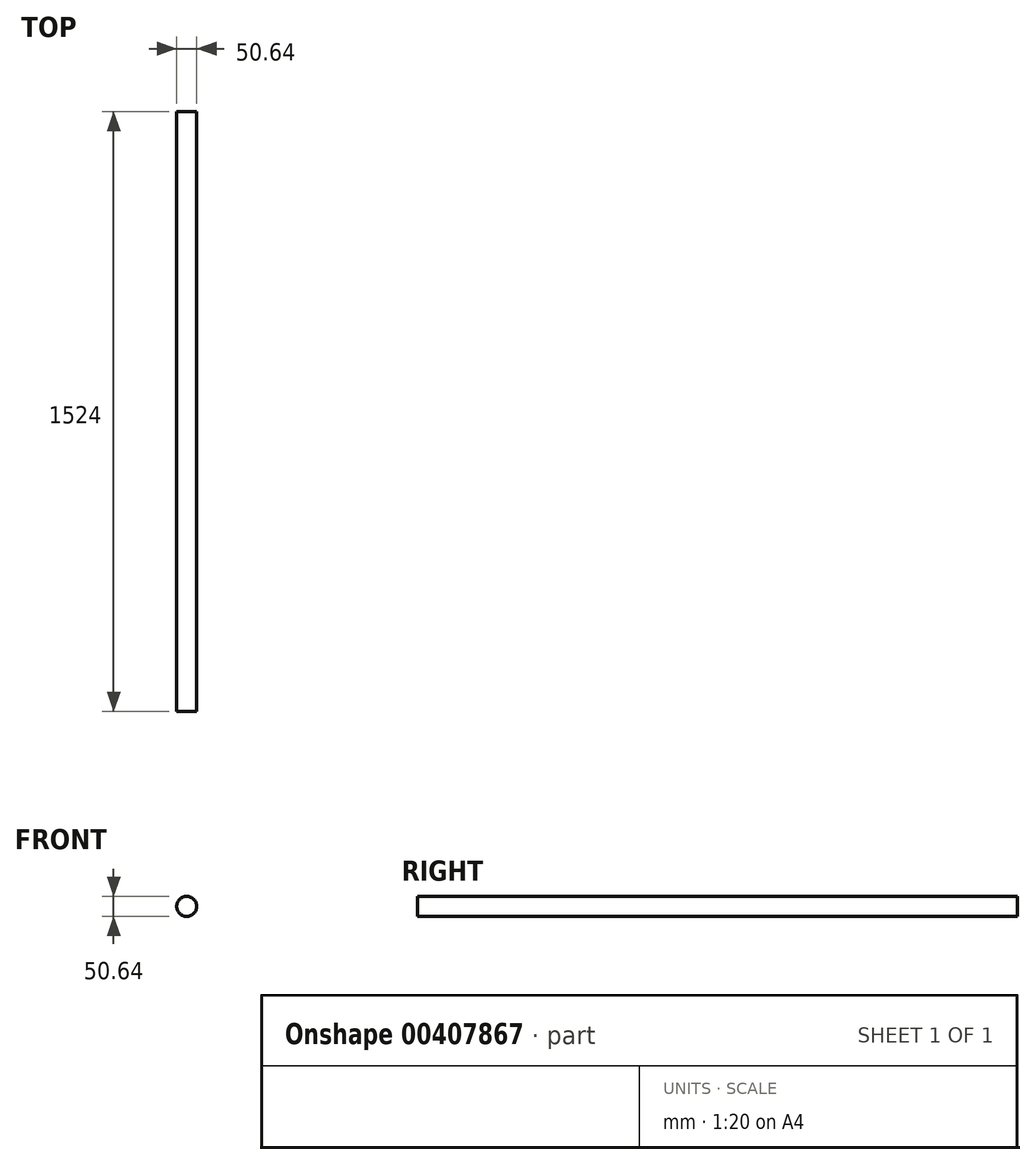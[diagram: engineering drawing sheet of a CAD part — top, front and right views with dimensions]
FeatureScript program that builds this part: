
annotation { "Feature Type Name" : "Feature", "Feature Type Description" : "" }
export const myFeature = defineFeature(function(context is Context, id is Id, definition is map)
    precondition{}
    {
        {
            var Q0;
            Q0=qCreatedBy(makeId("Front.planeOp"),FACE);
            var sketch = newSketch(context, id + "F0", { "sketchPlane" : qUnion([Q0])});
            skCircle(sketch, "E0", {"center": v(0, 0) * mm, "radius": 25.32 * mm});
            skCircle(sketch, "E1", {"center": v(-76.15, 16.15) * mm, "radius": 25.32 * mm});
            skSolve(sketch);
        }
        {
            var Q0;
            Q0=makeQuery(id+"F0.imprint","IMPRINT",FACE,{"disambiguationData":[TD([[makeQuery(id+"F0.imprint","IMPRINT",EDGE,{"derivedFrom":sQuery(id+"F0.wireOp",EDGE,"E0")}),1.0]])]});
            extrude(context, id + "F1", {"entities" : qUnion([Q0]), "depth" : 1524 * mm});
        }
    });
